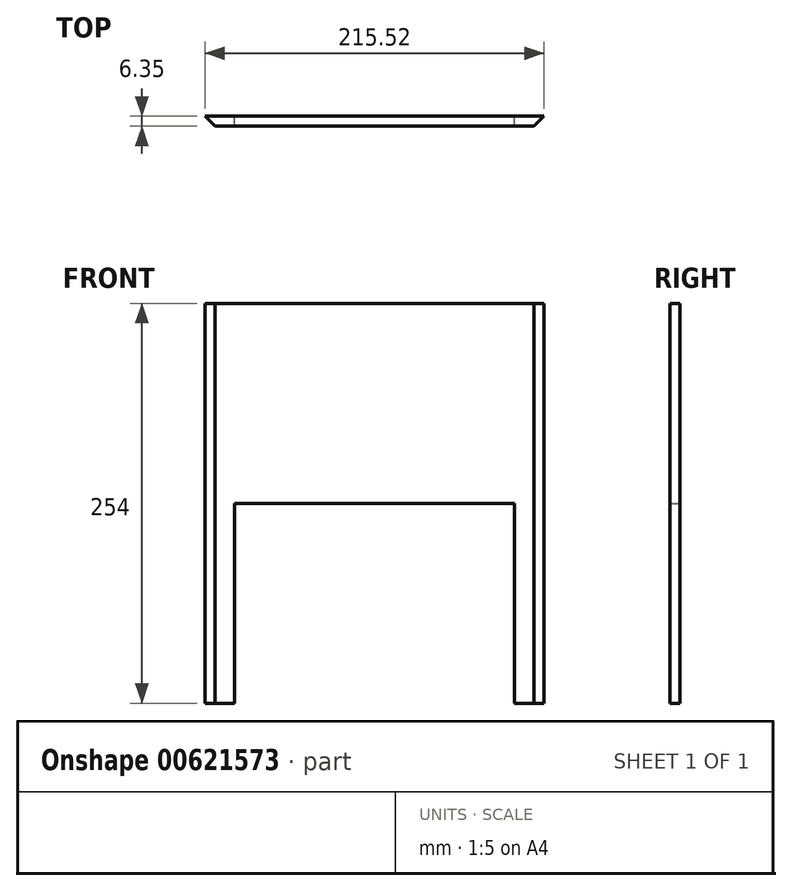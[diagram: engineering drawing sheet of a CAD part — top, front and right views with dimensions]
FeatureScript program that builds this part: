
annotation { "Feature Type Name" : "Feature", "Feature Type Description" : "" }
export const myFeature = defineFeature(function(context is Context, id is Id, definition is map)
    precondition{}
    {
        {
            var Q0;
            Q0=qCreatedBy(makeId("Front.planeOp"),FACE);
            var sketch = newSketch(context, id + "F0", { "sketchPlane" : qUnion([Q0])});
            skLineSegment(sketch, "E0.bottom", {"start": v(107.76, 127) * mm, "end": v(-107.76, 127) * mm});
            skLineSegment(sketch, "E0.top", {"start": v(107.76, -127) * mm, "end": v(-107.76, -127) * mm});
            skLineSegment(sketch, "E0.left", {"start": v(107.76, 127) * mm, "end": v(107.76, -127) * mm});
            skLineSegment(sketch, "E0.right", {"start": v(-107.76, 127) * mm, "end": v(-107.76, -127) * mm});
            skPoint(sketch, "E0.middle", {"position": v(0, 0) * mm});
            skSolve(sketch);
        }
        {
            var Q0;
            Q0 = qSketchRegion(id + "F0", true);
            extrude(context, id + "F1", {"entities" : qUnion([Q0]), "depth" : 6.35 * mm, "offsetDistance" : 25.4 * mm});
        }
        {
            var Q0;
            Q0=makeQuery(id+"F1.opExtrude","SWEPT_FACE",FACE,{"disambiguationData":[OSD([sQuery(id+"F0.wireOp",EDGE,"E0.bottom")])]});
            var sketch = newSketch(context, id + "F2", { "sketchPlane" : qUnion([Q0])});
            skLineSegment(sketch, "E1.bottom", {"start": v(-107.76, -6.35) * mm, "end": v(107.76, -6.35) * mm});
            skLineSegment(sketch, "E1.top", {"start": v(-107.76, 0) * mm, "end": v(107.76, 0) * mm});
            skLineSegment(sketch, "E1.left", {"start": v(-107.76, -6.35) * mm, "end": v(-107.76, 0) * mm});
            skLineSegment(sketch, "E1.right", {"start": v(107.76, -6.35) * mm, "end": v(107.76, 0) * mm});
            skLineSegment(sketch, "E2", {"start": v(-107.76, 0) * mm, "end": v(-101.41, -6.35) * mm});
            skLineSegment(sketch, "E3", {"start": v(107.76, 0) * mm, "end": v(101.41, -6.35) * mm});
            skSolve(sketch);
        }
        {
            var Q0;
            {var subQ0=sQuery(id+"F2.wireOp",EDGE,"E1.left");Q0=makeQuery(id+"F2.imprint","IMPRINT",FACE,{"disambiguationData":[TD([[makeQuery(id+"F2.imprint","IMPRINT",EDGE,{"derivedFrom":subQ0}),-1.0]])]});}
            var Q1;
            {var subQ0=sQuery(id+"F2.wireOp",EDGE,"E1.right");Q1=makeQuery(id+"F2.imprint","IMPRINT",FACE,{"disambiguationData":[TD([[makeQuery(id+"F2.imprint","IMPRINT",EDGE,{"derivedFrom":subQ0}),1.0]])]});}
            extrude(context, id + "F3", {"entities" : qUnion([Q0, Q1]), "operationType" : NewBodyOperationType.REMOVE, "endBound" : BoundingType.THROUGH_ALL, "oppositeDirection" : true, "depth" : 25.4 * mm, "offsetDistance" : 25.4 * mm});
        }
        {
            var Q0;
            Q0=makeQuery(id+"F1.opExtrude","CAP_FACE",FACE,{"disambiguationData":[OSD([sQuery(id+"F0.wireOp",EDGE,"E0.bottom"),sQuery(id+"F0.wireOp",EDGE,"E0.top"),sQuery(id+"F0.wireOp",EDGE,"E0.left"),sQuery(id+"F0.wireOp",EDGE,"E0.right")])],"isStart":true});
            var sketch = newSketch(context, id + "F4", { "sketchPlane" : qUnion([Q0])});
            skLineSegment(sketch, "E4", {"start": v(0, 0) * mm, "end": v(88.9, 0) * mm});
            skLineSegment(sketch, "E5.bottom", {"start": v(88.9, 0) * mm, "end": v(-88.9, 0) * mm});
            skLineSegment(sketch, "E5.top", {"start": v(88.9, -127) * mm, "end": v(-88.9, -127) * mm});
            skLineSegment(sketch, "E5.left", {"start": v(88.9, 0) * mm, "end": v(88.9, -127) * mm});
            skLineSegment(sketch, "E5.right", {"start": v(-88.9, 0) * mm, "end": v(-88.9, -127) * mm});
            skSolve(sketch);
        }
        {
            var Q0;
            Q0=makeQuery(id+"F4.imprint","IMPRINT",FACE,{"disambiguationData":[TD([[makeQuery(id+"F4.imprint","IMPRINT",EDGE,{"derivedFrom":sQuery(id+"F4.wireOp",EDGE,"E5.top")}),1.0]])]});
            extrude(context, id + "F5", {"entities" : qUnion([Q0]), "operationType" : NewBodyOperationType.REMOVE, "oppositeDirection" : true, "depth" : 25.4 * mm, "offsetDistance" : 25.4 * mm});
        }
    });
